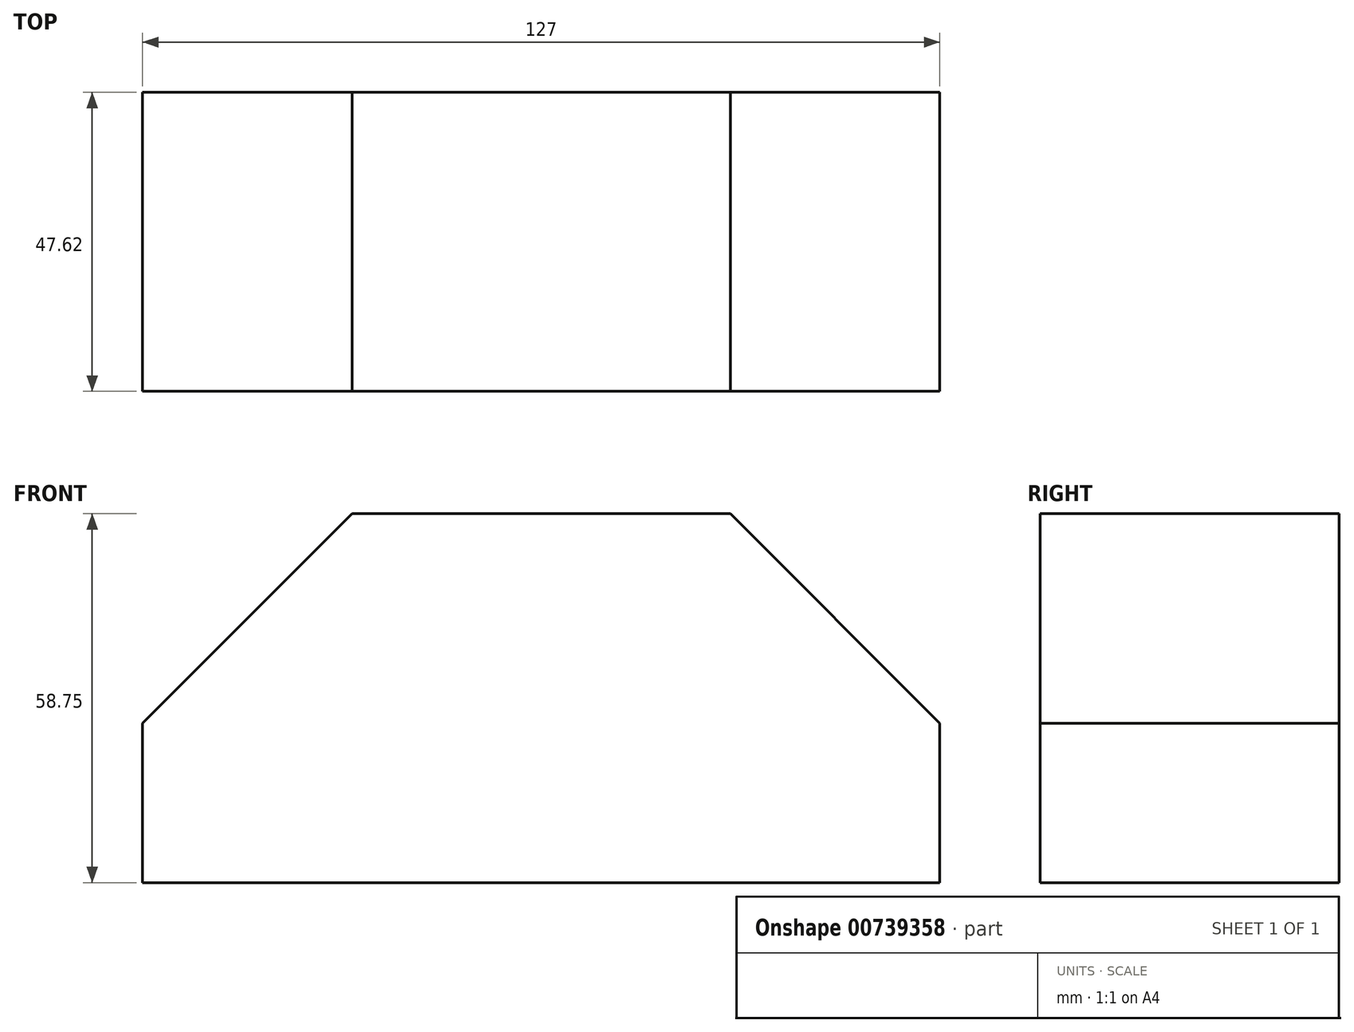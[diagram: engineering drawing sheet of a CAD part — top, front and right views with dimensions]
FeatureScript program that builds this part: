
annotation { "Feature Type Name" : "Feature", "Feature Type Description" : "" }
export const myFeature = defineFeature(function(context is Context, id is Id, definition is map)
    precondition{}
    {
        {
            var Q0;
            Q0=qCreatedBy(makeId("Front.planeOp"),FACE);
            var sketch = newSketch(context, id + "F0", { "sketchPlane" : qUnion([Q0])});
            skLineSegment(sketch, "E0", {"start": v(0, 0) * mm, "end": v(-127, 0) * mm});
            skLineSegment(sketch, "E1", {"start": v(-127, 0) * mm, "end": v(-127, 25.4) * mm});
            skLineSegment(sketch, "E2", {"start": v(-127, 25.4) * mm, "end": v(-93.65, 58.75) * mm});
            skLineSegment(sketch, "E3", {"start": v(-93.65, 58.75) * mm, "end": v(-33.35, 58.75) * mm});
            skLineSegment(sketch, "E4", {"start": v(-33.35, 58.75) * mm, "end": v(0, 25.4) * mm});
            skLineSegment(sketch, "E5", {"start": v(0, 25.4) * mm, "end": v(0, 0) * mm});
            skSolve(sketch);
        }
        {
            var Q0;
            Q0=makeQuery(id+"F0.imprint","IMPRINT",FACE,{"disambiguationData":[TD([[makeQuery(id+"F0.imprint","IMPRINT",EDGE,{"derivedFrom":sQuery(id+"F0.wireOp",EDGE,"E0")}),-1.0]])]});
            extrude(context, id + "F1", {"entities" : qUnion([Q0]), "depth" : 47.62 * mm, "offsetDistance" : 25.4 * mm});
        }
    });
